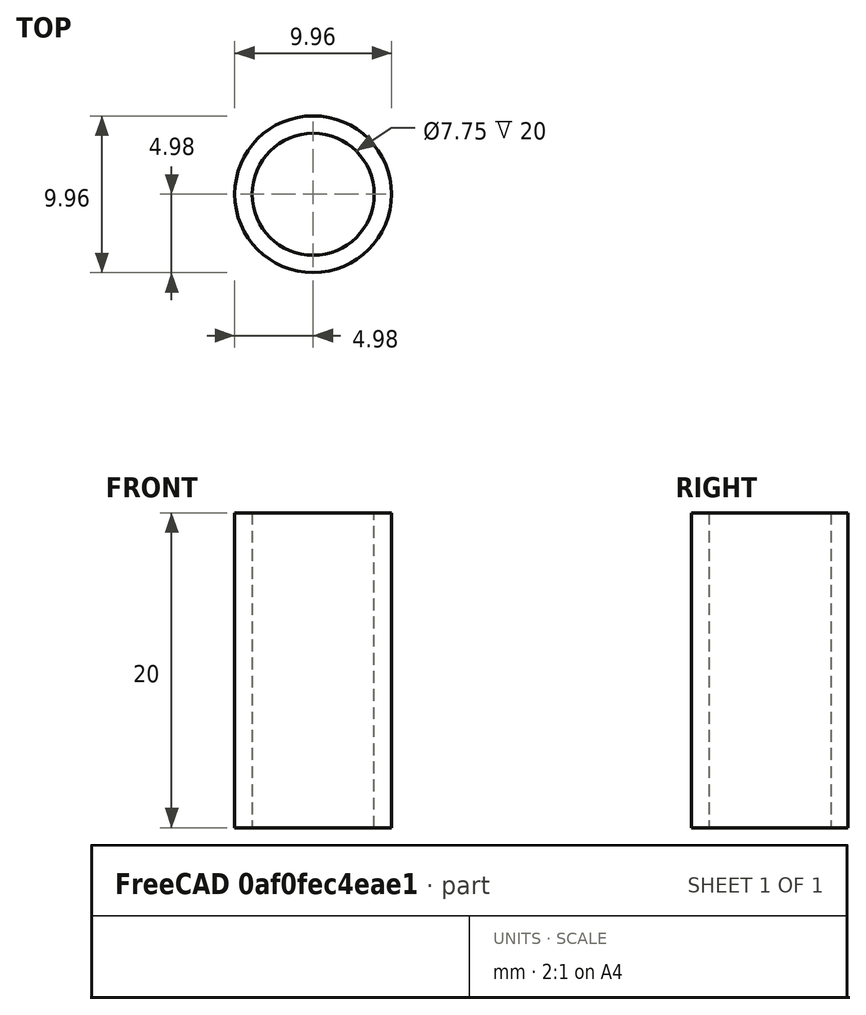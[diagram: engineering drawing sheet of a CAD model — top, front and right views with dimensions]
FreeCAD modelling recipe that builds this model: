
FCSTD DOCUMENT  (FreeCAD 0.18R16146 (Git))
Label: bolt sleeve 20mm
License: All rights reserved
LicenseURL: http://en.wikipedia.org/wiki/All_rights_reserved
objects: Sketcher::SketchObject×1, PartDesign::Pad×1, PartDesign::Body×1
note: 4 computed .brp shape members not serialized (recipe doc carries the construction recipe); baked Part::Feature solids carry a one-line shape summary decoded from their .brp

FEATURE [Sketcher::SketchObject] Sketch
  MapMode = 5
  Support = -> [XY_Plane]
  sketch-geometry (2):
    g0: Circle CenterX=0 CenterY=0 CenterZ=0 NormalX=0 NormalY=0 NormalZ=1 AngleXU=0 Radius=3.875
    g1: Circle CenterX=0 CenterY=0 CenterZ=0 NormalX=0 NormalY=0 NormalZ=1 AngleXU=0 Radius=4.98
  constraints (4):
    c: Coincident(g0,g-1)
    c: Coincident(g1,g0)
    c: Diameter(g0) = 7.75
    c: Diameter(g1) = 9.96
FEATURE [PartDesign::Pad] Pad
  Length = 20
  Length2 = 100
  Profile = -> Sketch
  Type = 0
FEATURE [PartDesign::Body] Body
  Group = -> [Sketch,Pad]
  Origin = -> Origin
  Tip = -> Pad
